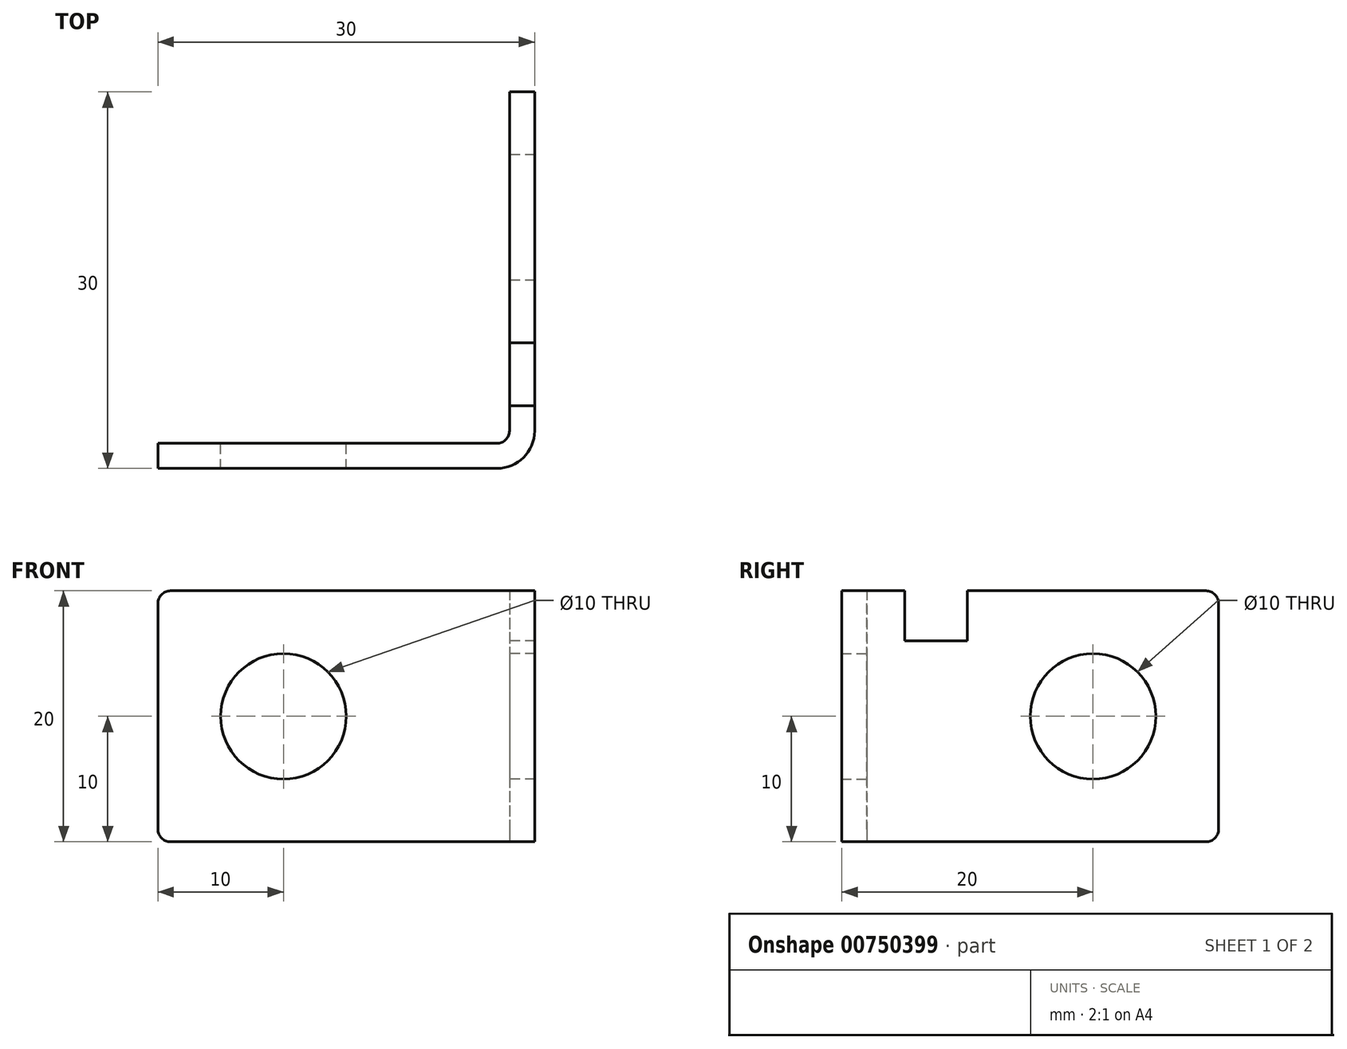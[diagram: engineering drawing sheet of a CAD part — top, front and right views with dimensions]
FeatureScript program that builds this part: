
annotation { "Feature Type Name" : "Feature", "Feature Type Description" : "" }
export const myFeature = defineFeature(function(context is Context, id is Id, definition is map)
    precondition{}
    {
        {
            var Q0;
            Q0=qCreatedBy(makeId("Front.planeOp"),FACE);
            var sketch = newSketch(context, id + "F0", { "sketchPlane" : qUnion([Q0])});
            skLineSegment(sketch, "E0.bottom", {"start": v(0, 0) * mm, "end": v(30, 0) * mm});
            skLineSegment(sketch, "E0.top", {"start": v(0, 20) * mm, "end": v(30, 20) * mm});
            skLineSegment(sketch, "E0.left", {"start": v(0, 0) * mm, "end": v(0, 20) * mm});
            skLineSegment(sketch, "E0.right", {"start": v(30, 0) * mm, "end": v(30, 20) * mm});
            skSolve(sketch);
        }
        {
            var Q0;
            Q0 = qSketchRegion(id + "F0", true);
            extrude(context, id + "F1", {"entities" : qUnion([Q0]), "oppositeDirection" : true, "depth" : 2 * mm, "offsetDistance" : 25 * mm});
        }
        {
            var Q0;
            Q0=makeQuery(id+"F1.opExtrude","CAP_FACE",FACE,{"disambiguationData":[OSD([sQuery(id+"F0.wireOp",EDGE,"E0.bottom"),sQuery(id+"F0.wireOp",EDGE,"E0.top"),sQuery(id+"F0.wireOp",EDGE,"E0.left"),sQuery(id+"F0.wireOp",EDGE,"E0.right")])],"isStart":true});
            var sketch = newSketch(context, id + "F2", { "sketchPlane" : qUnion([Q0])});
            skLineSegment(sketch, "E1.bottom", {"start": v(30, 20) * mm, "end": v(28, 20) * mm});
            skLineSegment(sketch, "E1.top", {"start": v(30, 0) * mm, "end": v(28, 0) * mm});
            skLineSegment(sketch, "E1.left", {"start": v(30, 20) * mm, "end": v(30, 0) * mm});
            skLineSegment(sketch, "E1.right", {"start": v(28, 20) * mm, "end": v(28, 0) * mm});
            skSolve(sketch);
        }
        {
            var Q0;
            Q0=makeQuery(id+"F2.imprint","IMPRINT",FACE,{"disambiguationData":[TD([[makeQuery(id+"F2.imprint","IMPRINT",EDGE,{"derivedFrom":sQuery(id+"F2.wireOp",EDGE,"E1.bottom")}),-1.0]])]});
            extrude(context, id + "F3", {"entities" : qUnion([Q0]), "operationType" : NewBodyOperationType.ADD, "oppositeDirection" : true, "depth" : 30 * mm, "offsetDistance" : 25 * mm});
        }
        {
            var Q0;
            Q0=makeQuery(id+"F1.opExtrude","CAP_FACE",FACE,{"disambiguationData":[OSD([sQuery(id+"F0.wireOp",EDGE,"E0.bottom"),sQuery(id+"F0.wireOp",EDGE,"E0.top"),sQuery(id+"F0.wireOp",EDGE,"E0.left"),sQuery(id+"F0.wireOp",EDGE,"E0.right")])],"isStart":false});
            var sketch = newSketch(context, id + "F4", { "sketchPlane" : qUnion([Q0])});
            skCircle(sketch, "E2", {"center": v(-10, 10) * mm, "radius": 5 * mm});
            skSolve(sketch);
        }
        {
            var Q0;
            Q0=makeQuery(id+"F3.opExtrude","SWEPT_FACE",FACE,{"disambiguationData":[OSD([sQuery(id+"F2.wireOp",EDGE,"E1.right")])]});
            var sketch = newSketch(context, id + "F5", { "sketchPlane" : qUnion([Q0])});
            skCircle(sketch, "E3", {"center": v(-20, 10) * mm, "radius": 5 * mm});
            skLineSegment(sketch, "E4.bottom", {"start": v(-5, 20) * mm, "end": v(-10, 20) * mm});
            skLineSegment(sketch, "E4.top", {"start": v(-5, 16) * mm, "end": v(-10, 16) * mm});
            skLineSegment(sketch, "E4.left", {"start": v(-5, 20) * mm, "end": v(-5, 16) * mm});
            skLineSegment(sketch, "E4.right", {"start": v(-10, 20) * mm, "end": v(-10, 16) * mm});
            skSolve(sketch);
        }
        {
            var Q0;
            Q0=makeQuery(id+"F5.imprint","IMPRINT",FACE,{"disambiguationData":[TD([[makeQuery(id+"F5.imprint","IMPRINT",EDGE,{"derivedFrom":sQuery(id+"F5.wireOp",EDGE,"E3")}),1.0]])]});
            var Q1;
            Q1=makeQuery(id+"F5.imprint","IMPRINT",FACE,{"disambiguationData":[TD([[makeQuery(id+"F5.imprint","IMPRINT",EDGE,{"derivedFrom":sQuery(id+"F5.wireOp",EDGE,"E4.bottom")}),-1.0]])]});
            extrude(context, id + "F6", {"entities" : qUnion([Q0, Q1]), "operationType" : NewBodyOperationType.REMOVE, "endBound" : BoundingType.THROUGH_ALL, "oppositeDirection" : true, "depth" : 25 * mm, "offsetDistance" : 25 * mm});
        }
        {
            var Q0;
            Q0 = qSketchRegion(id + "F4", true);
            extrude(context, id + "F7", {"entities" : qUnion([Q0]), "operationType" : NewBodyOperationType.REMOVE, "oppositeDirection" : true, "depth" : 25 * mm, "offsetDistance" : 25 * mm});
        }
        {
            var Q0;
            Q0=makeQuery(id+"F1.opExtrude","CAP_EDGE",EDGE,{"disambiguationData":[OSD([sQuery(id+"F0.wireOp",EDGE,"E0.right")])],"isStart":true});
            fillet(context, id + "F8", {"entities" : qUnion([Q0]), "radius" : 3 * mm, "tangentPropagation" : true, "allowEdgeOverflow" : false});
        }
        {
            var Q0;
            Q0=makeQuery(id+"F1.opExtrude","SWEPT_EDGE",EDGE,{"disambiguationData":[OSD([sQuery(id+"F0.wireOp",EDGE,"E0.top"),sQuery(id+"F0.wireOp",EDGE,"E0.left")])]});
            var Q1;
            Q1=makeQuery(id+"F3.boolean.opBoolean","INTERSECT",EDGE,{"derivedFrom":[makeQuery(id+"F1.opExtrude","CAP_FACE",FACE,{"disambiguationData":[OSD([sQuery(id+"F0.wireOp",EDGE,"E0.bottom"),sQuery(id+"F0.wireOp",EDGE,"E0.top"),sQuery(id+"F0.wireOp",EDGE,"E0.left"),sQuery(id+"F0.wireOp",EDGE,"E0.right")])],"isStart":false}),makeQuery(id+"F3.opExtrude","SWEPT_FACE",FACE,{"disambiguationData":[OSD([sQuery(id+"F2.wireOp",EDGE,"E1.right")])]})]});
            var Q2;
            Q2=makeQuery(id+"F3.opExtrude","CAP_EDGE",EDGE,{"disambiguationData":[OSD([sQuery(id+"F2.wireOp",EDGE,"E1.bottom")])],"isStart":false});
            var Q3;
            Q3=makeQuery(id+"F1.opExtrude","SWEPT_EDGE",EDGE,{"disambiguationData":[OSD([sQuery(id+"F0.wireOp",EDGE,"E0.bottom"),sQuery(id+"F0.wireOp",EDGE,"E0.left")])]});
            var Q4;
            Q4=makeQuery(id+"F3.opExtrude","CAP_EDGE",EDGE,{"disambiguationData":[OSD([sQuery(id+"F2.wireOp",EDGE,"E1.top")])],"isStart":false});
            fillet(context, id + "F9", {"entities" : qUnion([Q0, Q1, Q2, Q3, Q4]), "radius" : 1 * mm, "tangentPropagation" : true, "allowEdgeOverflow" : false});
        }
    });
